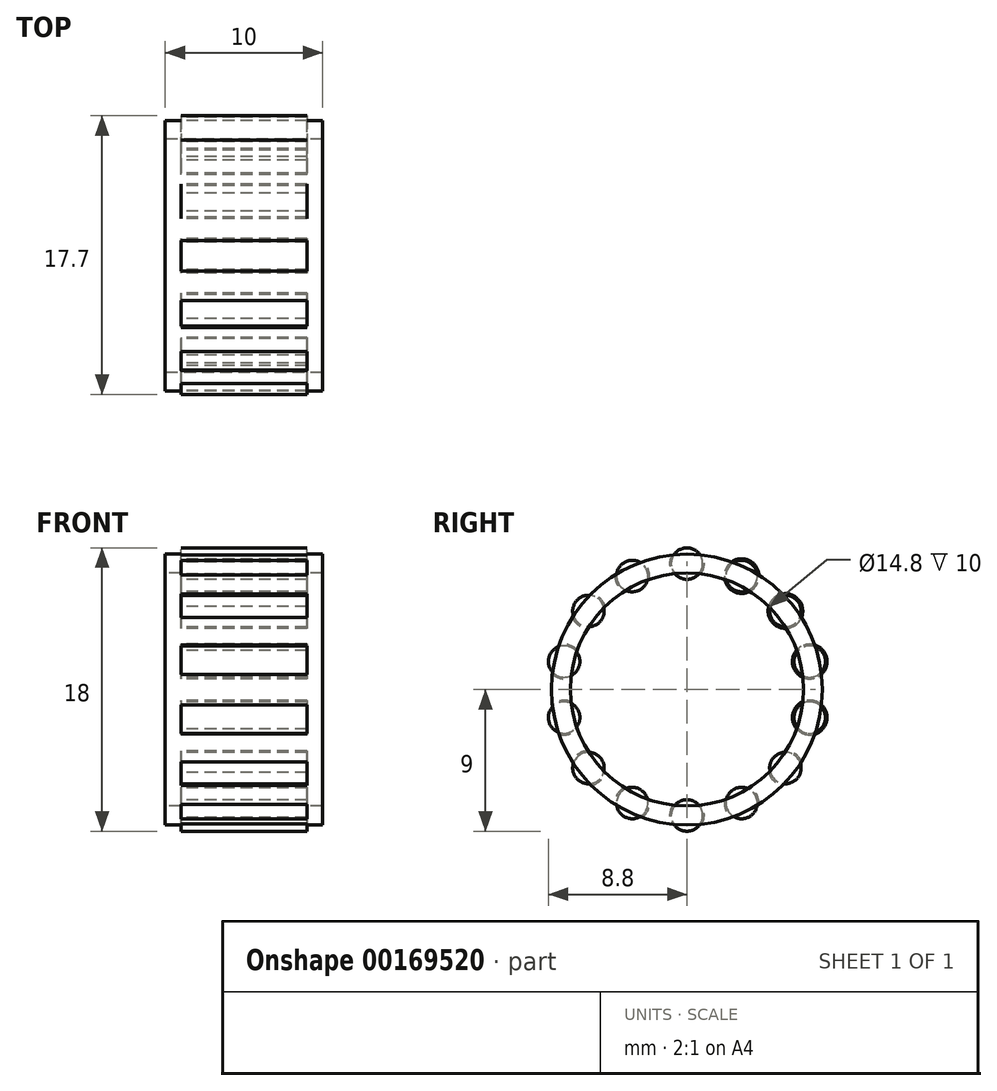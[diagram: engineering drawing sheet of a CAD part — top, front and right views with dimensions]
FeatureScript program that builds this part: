
annotation { "Feature Type Name" : "Feature", "Feature Type Description" : "" }
export const myFeature = defineFeature(function(context is Context, id is Id, definition is map)
    precondition{}
    {
        {
            assignVariable(context, id + "F0", {"name" : "Width", "anyValue" : 10});
        }
        {
            assignVariable(context, id + "F1", {"name" : "NumNeedles", "anyValue" : 14});
        }
        {
            var Q0;
            Q0=qCreatedBy(makeId("Right.planeOp"),FACE);
            var sketch = newSketch(context, id + "F2", { "sketchPlane" : qUnion([Q0])});
            skCircle(sketch, "E0", {"center": v(0, 0) * mm, "radius": 7 * mm, "construction": true});
            skCircle(sketch, "E1", {"center": v(0, 0) * mm, "radius": 7.4 * mm});
            skCircle(sketch, "E2", {"center": v(0, 0) * mm, "radius": 8.6 * mm});
            skSolve(sketch);
        }
        {
            var Q0;
            Q0 = qSketchRegion(id + "F2", true);
            extrude(context, id + "F3", {"entities" : qUnion([Q0]), "endBound" : BoundingType.SYMMETRIC, "depth" : (getVariable(context, 'Width')) * mm});
        }
        {
            var Q0;
            Q0=qCreatedBy(makeId("Right.planeOp"),FACE);
            var sketch = newSketch(context, id + "F4", { "sketchPlane" : qUnion([Q0])});
            skCircle(sketch, "E3", {"center": v(0, 8) * mm, "radius": 1.1 * mm});
            skSolve(sketch);
        }
        {
            var Q0;
            Q0 = qSketchRegion(id + "F4", true);
            extrude(context, id + "F5", {"entities" : qUnion([Q0]), "endBound" : BoundingType.SYMMETRIC, "depth" : (getVariable(context, 'Width') - 2 * 1) * mm});
        }
        {
            var Q0;
            Q0=makeQuery(id+"F5.opExtrude","SWEPT_BODY",BODY,{"disambiguationData":[OSD([sQuery(id+"F4.wireOp",EDGE,"E3")])]});
            var Q1;
            Q1=makeQuery(id+"F3.opExtrude","CAP_EDGE",EDGE,{"disambiguationData":[OSD([sQuery(id+"F2.wireOp",EDGE,"E1")])],"isStart":false});
            circularPattern(context, id + "F6", {"entities" : qUnion([Q0]), "axis" : qUnion([Q1]), "angle" : 360 * degree, "instanceCount" : getVariable(context, 'NumNeedles'), "equalSpace" : true});
        }
        {
            var Q0;
            Q0=makeQuery(id+"F6.opPattern","COPY",BODY,{"derivedFrom":makeQuery(id+"F5.opExtrude","SWEPT_BODY",BODY,{"disambiguationData":[OSD([sQuery(id+"F4.wireOp",EDGE,"E3")])]}),"instanceName":"1"});
            var Q1;
            Q1=makeQuery(id+"F6.opPattern","COPY",BODY,{"derivedFrom":makeQuery(id+"F5.opExtrude","SWEPT_BODY",BODY,{"disambiguationData":[OSD([sQuery(id+"F4.wireOp",EDGE,"E3")])]}),"instanceName":"4"});
            var Q2;
            Q2=makeQuery(id+"F6.opPattern","COPY",BODY,{"derivedFrom":makeQuery(id+"F5.opExtrude","SWEPT_BODY",BODY,{"disambiguationData":[OSD([sQuery(id+"F4.wireOp",EDGE,"E3")])]}),"instanceName":"9"});
            var Q3;
            Q3=makeQuery(id+"F6.opPattern","COPY",BODY,{"derivedFrom":makeQuery(id+"F5.opExtrude","SWEPT_BODY",BODY,{"disambiguationData":[OSD([sQuery(id+"F4.wireOp",EDGE,"E3")])]}),"instanceName":"3"});
            var Q4;
            Q4=makeQuery(id+"F6.opPattern","COPY",BODY,{"derivedFrom":makeQuery(id+"F5.opExtrude","SWEPT_BODY",BODY,{"disambiguationData":[OSD([sQuery(id+"F4.wireOp",EDGE,"E3")])]}),"instanceName":"5"});
            var Q5;
            Q5=makeQuery(id+"F6.opPattern","COPY",BODY,{"derivedFrom":makeQuery(id+"F5.opExtrude","SWEPT_BODY",BODY,{"disambiguationData":[OSD([sQuery(id+"F4.wireOp",EDGE,"E3")])]}),"instanceName":"2"});
            var Q6;
            Q6=makeQuery(id+"F6.opPattern","COPY",BODY,{"derivedFrom":makeQuery(id+"F5.opExtrude","SWEPT_BODY",BODY,{"disambiguationData":[OSD([sQuery(id+"F4.wireOp",EDGE,"E3")])]}),"instanceName":"7"});
            var Q7;
            Q7=makeQuery(id+"F6.opPattern","COPY",BODY,{"derivedFrom":makeQuery(id+"F5.opExtrude","SWEPT_BODY",BODY,{"disambiguationData":[OSD([sQuery(id+"F4.wireOp",EDGE,"E3")])]}),"instanceName":"8"});
            var Q8;
            Q8=makeQuery(id+"F6.opPattern","COPY",BODY,{"derivedFrom":makeQuery(id+"F5.opExtrude","SWEPT_BODY",BODY,{"disambiguationData":[OSD([sQuery(id+"F4.wireOp",EDGE,"E3")])]}),"instanceName":"6"});
            var Q9;
            Q9=makeQuery(id+"F5.opExtrude","SWEPT_BODY",BODY,{"disambiguationData":[OSD([sQuery(id+"F4.wireOp",EDGE,"E3")])]});
            var Q10;
            Q10=makeQuery(id+"F3.opExtrude","SWEPT_BODY",BODY,{"disambiguationData":[OSD([sQuery(id+"F2.wireOp",EDGE,"E1"),sQuery(id+"F2.wireOp",EDGE,"E2")])]});
            booleanBodies(context, id + "F7", {"operationType" : BooleanOperationType.SUBTRACTION, "tools" : qUnion([Q0, Q1, Q2, Q3, Q4, Q5, Q6, Q7, Q8, Q9]), "targets" : qUnion([Q10])});
        }
        {
            var Q0;
            Q0=qCreatedBy(makeId("Right.planeOp"),FACE);
            var sketch = newSketch(context, id + "F8", { "sketchPlane" : qUnion([Q0])});
            skCircle(sketch, "E4", {"center": v(0, 8) * mm, "radius": 1 * mm});
            skSolve(sketch);
        }
        {
            var Q0;
            Q0 = qSketchRegion(id + "F8", true);
            extrude(context, id + "F9", {"entities" : qUnion([Q0]), "endBound" : BoundingType.SYMMETRIC, "depth" : (getVariable(context, 'Width') - 2 * 1) * mm});
        }
        {
            var Q0;
            Q0=makeQuery(id+"F9.opExtrude","SWEPT_BODY",BODY,{"disambiguationData":[OSD([sQuery(id+"F8.wireOp",EDGE,"E4")])]});
            var Q1;
            Q1=makeQuery(id+"F3.opExtrude","CAP_EDGE",EDGE,{"disambiguationData":[OSD([sQuery(id+"F2.wireOp",EDGE,"E1")])],"isStart":false});
            circularPattern(context, id + "F10", {"entities" : qUnion([Q0]), "axis" : qUnion([Q1]), "angle" : 360 * degree, "instanceCount" : getVariable(context, 'NumNeedles'), "equalSpace" : true});
        }
    });
